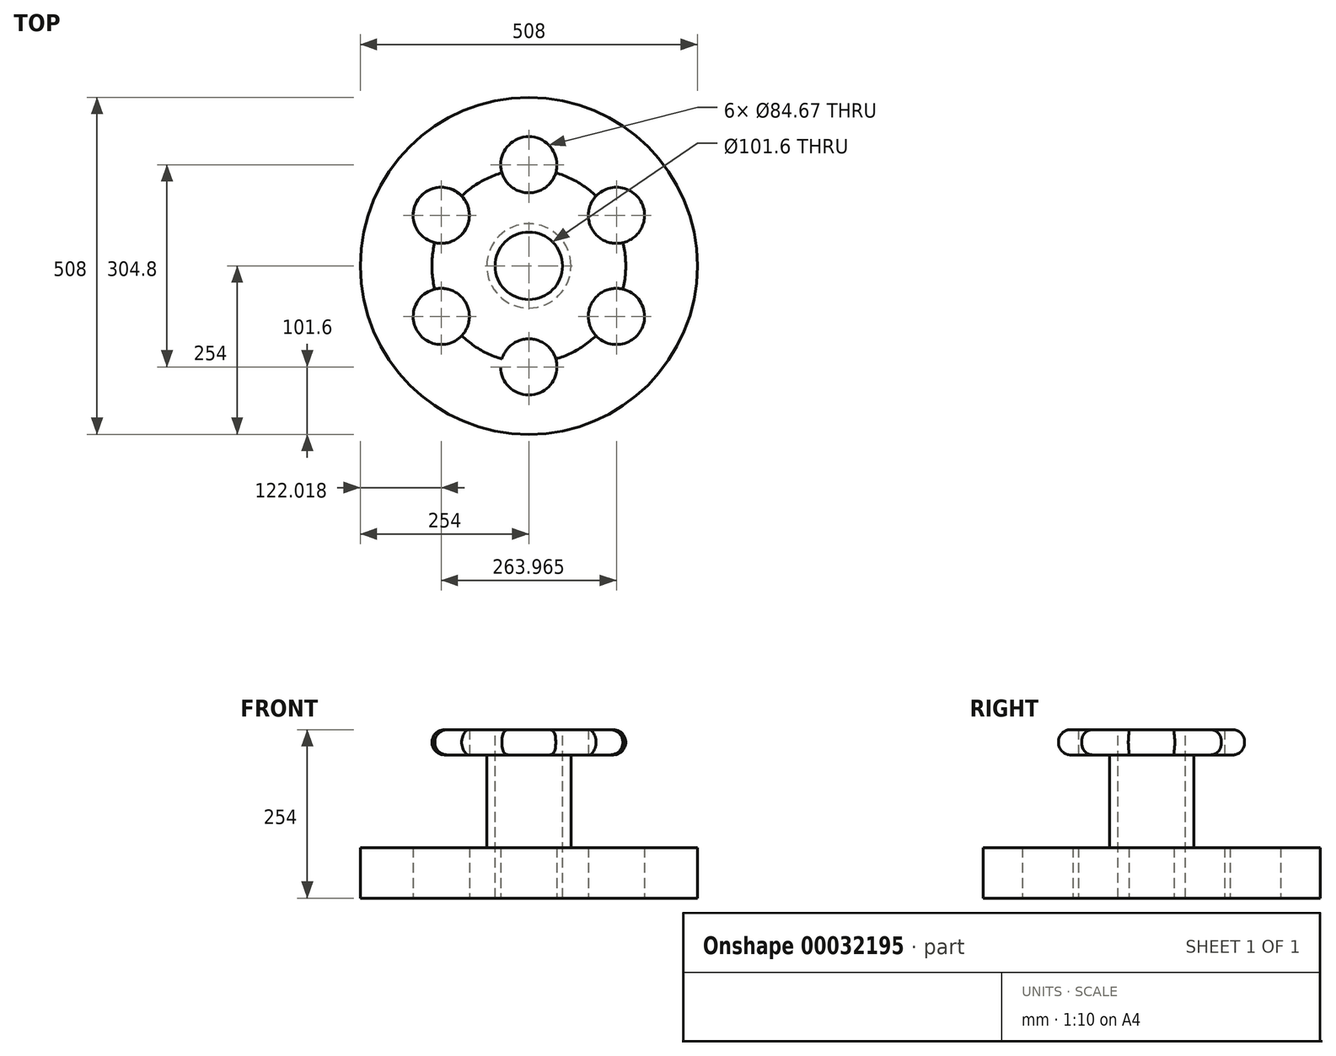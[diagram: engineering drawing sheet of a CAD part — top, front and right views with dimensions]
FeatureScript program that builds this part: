
annotation { "Feature Type Name" : "Feature", "Feature Type Description" : "" }
export const myFeature = defineFeature(function(context is Context, id is Id, definition is map)
    precondition{}
    {
        {
            var Q0;
            Q0=qCreatedBy(makeId("Front.planeOp"),FACE);
            var sketch = newSketch(context, id + "F0", { "sketchPlane" : qUnion([Q0])});
            skLineSegment(sketch, "E0", {"start": v(0, 272.53) * mm, "end": v(0, -289.46) * mm, "construction": true});
            skLineSegment(sketch, "E1", {"start": v(-50.8, 254) * mm, "end": v(-127, 254) * mm});
            skLineSegment(sketch, "E2", {"start": v(-127, 254) * mm, "end": v(-127, 215.9) * mm});
            skLineSegment(sketch, "E3", {"start": v(-127, 215.9) * mm, "end": v(-63.5, 215.9) * mm});
            skLineSegment(sketch, "E4", {"start": v(-63.5, 215.9) * mm, "end": v(-63.5, 76.2) * mm});
            skLineSegment(sketch, "E5", {"start": v(-63.5, 76.2) * mm, "end": v(-254, 76.2) * mm});
            skLineSegment(sketch, "E6", {"start": v(-254, 76.2) * mm, "end": v(-254, 0) * mm});
            skLineSegment(sketch, "E7", {"start": v(-254, 0) * mm, "end": v(-50.8, 0) * mm});
            skLineSegment(sketch, "E8", {"start": v(-50.8, 0) * mm, "end": v(-50.8, 254) * mm});
            skArc(sketch, "E9", {"start": v(-127, 254) * mm, "mid": v(-146.05, 234.95) * mm, "end": v(-127, 215.9) * mm});
            skSolve(sketch);
        }
        {
            var Q0;
            Q0=makeQuery(id+"F0.imprint","IMPRINT",FACE,{"disambiguationData":[TD([[makeQuery(id+"F0.imprint","IMPRINT",EDGE,{"derivedFrom":sQuery(id+"F0.wireOp",EDGE,"E1")}),1.0]])]});
            var Q1;
            Q1=makeQuery(id+"F0.imprint","IMPRINT",FACE,{"disambiguationData":[TD([[makeQuery(id+"F0.imprint","IMPRINT",EDGE,{"derivedFrom":sQuery(id+"F0.wireOp",EDGE,"E2")}),-1.0]])]});
            var Q2;
            Q2=makeQuery(id+"F0.imprint","IMPRINT",FACE,{"disambiguationData":[TD([[makeQuery(id+"F0.imprint","IMPRINT",EDGE,{"derivedFrom":sQuery(id+"F0.wireOp",EDGE,"E7")}),-1.0]])]});
            var Q3;
            Q3=sQuery(id+"F0.wireOp",EDGE,"E0");
            revolve(context, id + "F1", {"entities" : qUnion([Q0, Q1, Q2]), "axis" : qUnion([Q3]), "revolveType" : RevolveType.FULL});
        }
        {
            var Q0;
            Q0=makeQuery(id+"F1.opRevolve","SWEPT_FACE",FACE,{"disambiguationData":[OSD([sQuery(id+"F0.wireOp",EDGE,"E7")])]});
            var sketch = newSketch(context, id + "F2", { "sketchPlane" : qUnion([Q0])});
            skCircle(sketch, "E10", {"center": v(0, 0) * mm, "radius": 152.4 * mm, "construction": true});
            skCircle(sketch, "E11", {"center": v(0, 152.4) * mm, "radius": 42.33 * mm});
            skCircle(sketch, "E12.1.0", {"center": v(-131.98, 76.2) * mm, "radius": 42.33 * mm});
            skCircle(sketch, "E12.2.0", {"center": v(-131.98, -76.2) * mm, "radius": 42.33 * mm});
            skCircle(sketch, "E12.3.0", {"center": v(0, -152.4) * mm, "radius": 42.33 * mm});
            skCircle(sketch, "E12.4.0", {"center": v(131.98, -76.2) * mm, "radius": 42.33 * mm});
            skCircle(sketch, "E12.5.0", {"center": v(131.98, 76.2) * mm, "radius": 42.33 * mm});
            skSolve(sketch);
        }
        {
            var Q0;
            Q0 = qSketchRegion(id + "F2", true);
            extrude(context, id + "F3", {"entities" : qUnion([Q0]), "operationType" : NewBodyOperationType.REMOVE, "endBound" : BoundingType.THROUGH_ALL, "oppositeDirection" : true, "depth" : 25.4 * mm});
        }
    });
